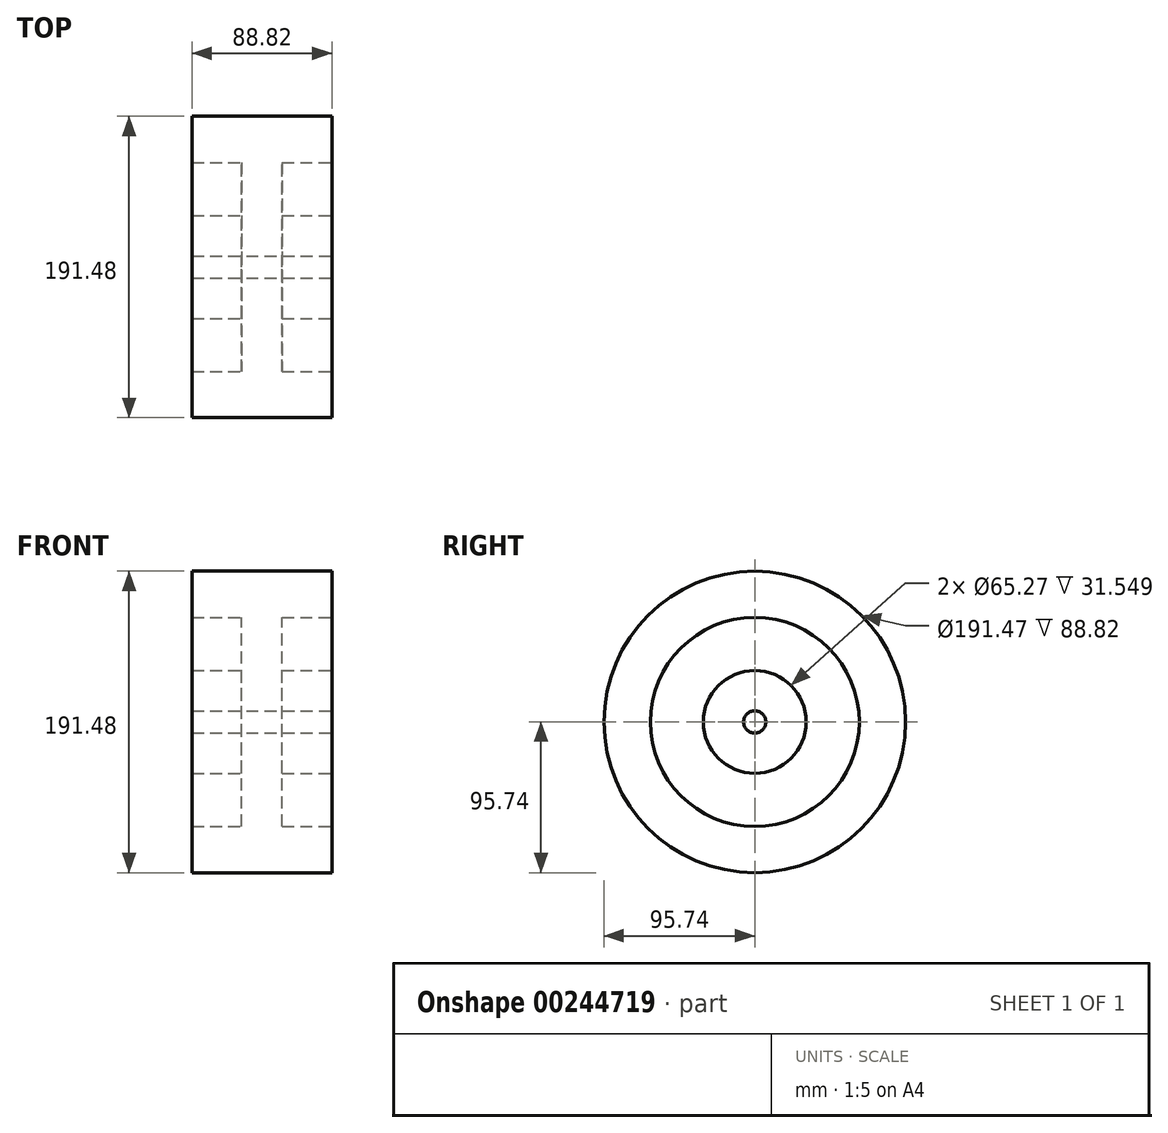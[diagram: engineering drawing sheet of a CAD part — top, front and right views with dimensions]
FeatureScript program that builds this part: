
annotation { "Feature Type Name" : "Feature", "Feature Type Description" : "" }
export const myFeature = defineFeature(function(context is Context, id is Id, definition is map)
    precondition{}
    {
        {
            var Q0;
            Q0=qCreatedBy(makeId("Front.planeOp"),FACE);
            var sketch = newSketch(context, id + "F0", { "sketchPlane" : qUnion([Q0])});
            skLineSegment(sketch, "E0", {"start": v(-164.9, 0) * mm, "end": v(167.46, 0) * mm, "construction": true});
            skLineSegment(sketch, "E1", {"start": v(-44.4, 95.74) * mm, "end": v(44.4, 95.74) * mm});
            skLineSegment(sketch, "E2", {"start": v(44.4, 95.74) * mm, "end": v(44.4, 66.36) * mm});
            skLineSegment(sketch, "E3", {"start": v(44.4, 66.36) * mm, "end": v(12.86, 66.36) * mm});
            skLineSegment(sketch, "E4", {"start": v(12.86, 66.36) * mm, "end": v(12.86, 32.64) * mm});
            skLineSegment(sketch, "E5", {"start": v(12.86, 32.64) * mm, "end": v(44.4, 32.64) * mm});
            skLineSegment(sketch, "E6", {"start": v(44.4, 32.64) * mm, "end": v(44.4, 7.07) * mm});
            skLineSegment(sketch, "E7", {"start": v(44.4, 7.07) * mm, "end": v(-44.4, 7.07) * mm});
            skLineSegment(sketch, "E8", {"start": v(-44.4, 7.07) * mm, "end": v(-44.4, 32.64) * mm});
            skLineSegment(sketch, "E9", {"start": v(-44.4, 32.64) * mm, "end": v(-12.86, 32.64) * mm});
            skLineSegment(sketch, "E10", {"start": v(-12.86, 32.64) * mm, "end": v(-12.86, 66.36) * mm});
            skLineSegment(sketch, "E11", {"start": v(-12.86, 66.36) * mm, "end": v(-44.4, 66.36) * mm});
            skLineSegment(sketch, "E12", {"start": v(-44.4, 66.36) * mm, "end": v(-44.4, 95.74) * mm});
            skLineSegment(sketch, "E13", {"start": v(0, 0) * mm, "end": v(0, 134.9) * mm, "construction": true});
            skSolve(sketch);
        }
        {
            var Q0;
            Q0=sQuery(id+"F0.wireOp",EDGE,"E11");
            var Q1;
            Q1=sQuery(id+"F0.wireOp",EDGE,"E5");
            var Q2;
            Q2=sQuery(id+"F0.wireOp",EDGE,"E10");
            var Q3;
            Q3=sQuery(id+"F0.wireOp",EDGE,"E12");
            var Q4;
            Q4=sQuery(id+"F0.wireOp",EDGE,"E1");
            var Q5;
            Q5=sQuery(id+"F0.wireOp",EDGE,"E9");
            var Q6;
            Q6=sQuery(id+"F0.wireOp",EDGE,"E6");
            var Q7;
            Q7=sQuery(id+"F0.wireOp",EDGE,"E3");
            var Q8;
            Q8=sQuery(id+"F0.wireOp",EDGE,"E7");
            var Q9;
            Q9=sQuery(id+"F0.wireOp",EDGE,"E8");
            var Q10;
            Q10=sQuery(id+"F0.wireOp",EDGE,"E4");
            var Q11;
            Q11=sQuery(id+"F0.wireOp",EDGE,"E2");
            var Q12;
            Q12=sQuery(id+"F0.wireOp",EDGE,"E0");
            revolve(context, id + "F1", {"bodyType" : ToolBodyType.SURFACE, "surfaceEntities" : qUnion([Q0, Q1, Q2, Q3, Q4, Q5, Q6, Q7, Q8, Q9, Q10, Q11]), "axis" : qUnion([Q12]), "revolveType" : RevolveType.FULL});
        }
    });
